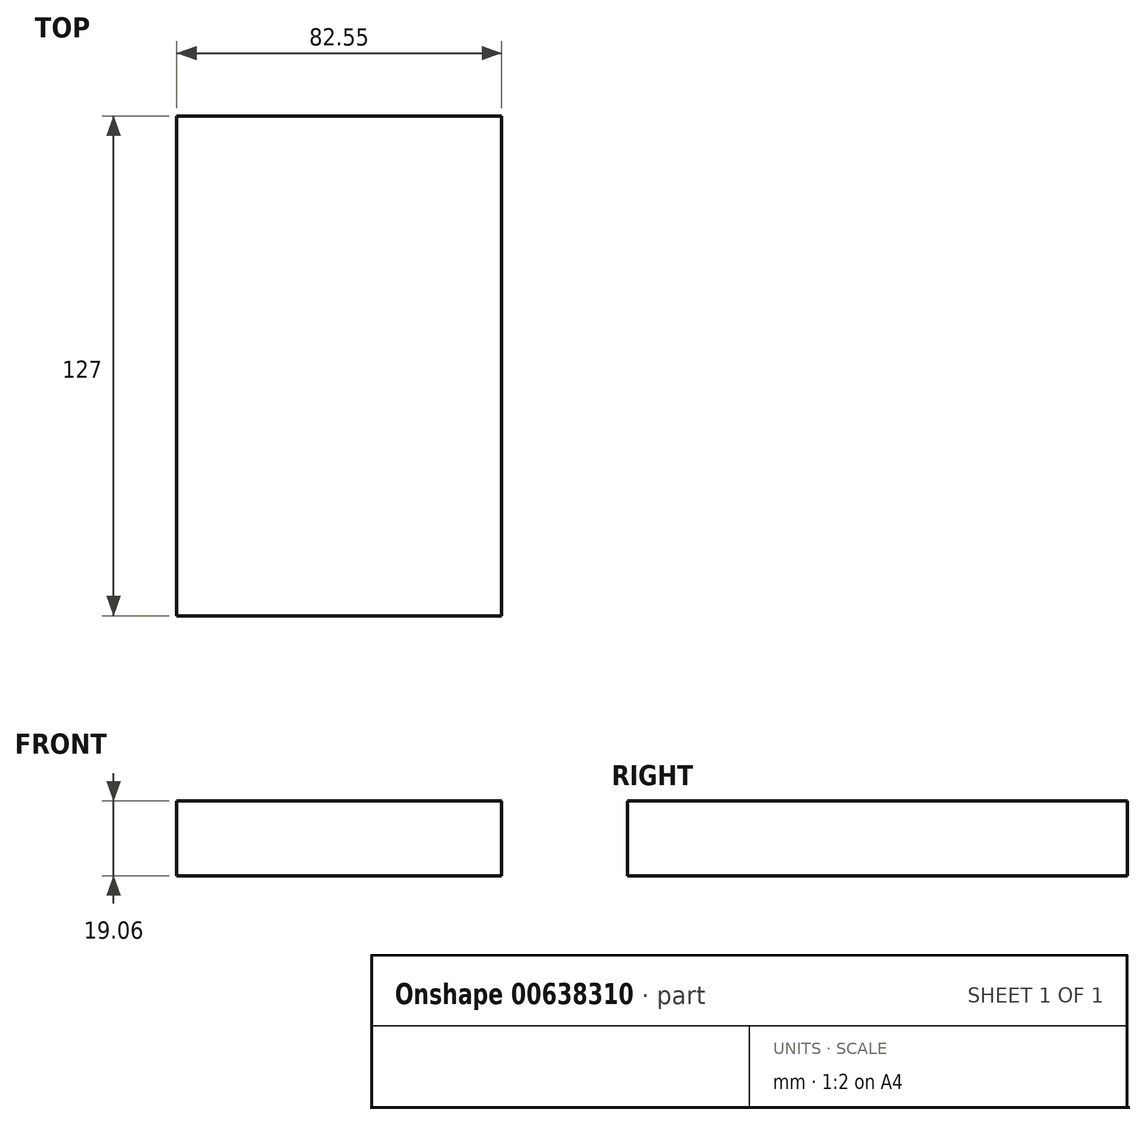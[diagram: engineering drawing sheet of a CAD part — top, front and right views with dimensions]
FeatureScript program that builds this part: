
annotation { "Feature Type Name" : "Feature", "Feature Type Description" : "" }
export const myFeature = defineFeature(function(context is Context, id is Id, definition is map)
    precondition{}
    {
        {
            var Q0;
            Q0=qCreatedBy(makeId("Front.planeOp"),FACE);
            var sketch = newSketch(context, id + "F0", { "sketchPlane" : qUnion([Q0])});
            skLineSegment(sketch, "E0.bottom", {"start": v(-41.28, 9.52) * mm, "end": v(41.28, 9.53) * mm});
            skLineSegment(sketch, "E0.top", {"start": v(-41.28, -9.53) * mm, "end": v(41.28, -9.53) * mm});
            skLineSegment(sketch, "E0.left", {"start": v(-41.28, 9.52) * mm, "end": v(-41.28, -9.53) * mm});
            skLineSegment(sketch, "E0.right", {"start": v(41.28, 9.53) * mm, "end": v(41.28, -9.52) * mm});
            skPoint(sketch, "E0.middle", {"position": v(0, 0) * mm});
            skLineSegment(sketch, "E1", {"start": v(41.27, 9.53) * mm, "end": v(41.27, 27) * mm});
            skLineSegment(sketch, "E2.bottom", {"start": v(60.32, 38.1) * mm, "end": v(111.12, 38.1) * mm});
            skLineSegment(sketch, "E2.top", {"start": v(60.32, 66.68) * mm, "end": v(111.12, 66.68) * mm});
            skLineSegment(sketch, "E2.left", {"start": v(60.32, 38.1) * mm, "end": v(60.32, 66.67) * mm});
            skLineSegment(sketch, "E2.right", {"start": v(111.12, 38.1) * mm, "end": v(111.12, 66.68) * mm});
            skPoint(sketch, "E2.middle", {"position": v(85.72, 52.39) * mm});
            skArc(sketch, "E3", {"start": v(41.27, 27) * mm, "mid": v(45.92, 38.23) * mm, "end": v(57.15, 42.88) * mm});
            skLineSegment(sketch, "E4", {"start": v(57.15, 42.88) * mm, "end": v(78.18, 42.88) * mm});
            skLineSegment(sketch, "E5.0", {"start": v(57.15, 61.93) * mm, "end": v(78.18, 61.93) * mm});
            skArc(sketch, "E5.1", {"start": v(22.22, 27) * mm, "mid": v(32.45, 51.7) * mm, "end": v(57.15, 61.93) * mm});
            skLineSegment(sketch, "E5.2", {"start": v(22.22, 9.53) * mm, "end": v(22.22, 27) * mm});
            skLineSegment(sketch, "E6", {"start": v(85.72, 38.1) * mm, "end": v(85.72, 66.68) * mm});
            skLineSegment(sketch, "E7", {"start": v(78.18, 61.93) * mm, "end": v(85.72, 61.93) * mm});
            skFitSpline(sketch, "E8", {"points": [v(-41.28, 9.52) * mm, v(57.15, 61.93) * mm], "startDerivative": vector(34.3, 92.65) * mm, "endDerivative": vector(125.6, -3.99) * mm});
            skSolve(sketch);
        }
        {
            var Q0;
            Q0=makeQuery(id+"F0.imprint","IMPRINT",FACE,{"disambiguationData":[TD([[makeQuery(id+"F0.imprint","IMPRINT",EDGE,{"derivedFrom":sQuery(id+"F0.wireOp",EDGE,"E0.top")}),1.0]])]});
            extrude(context, id + "F1", {"entities" : qUnion([Q0]), "depth" : 127 * mm, "offsetDistance" : 25.4 * mm});
        }
    });
